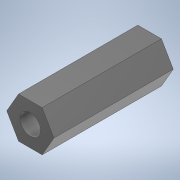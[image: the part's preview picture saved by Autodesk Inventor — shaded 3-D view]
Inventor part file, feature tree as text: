
AUTODESK INVENTOR PART (.ipt)
format: ipt  version: 2020 (Build 240168000, 168)  size: 103,936 bytes
history: native  units: mm
features: extrude x1, sketch x1
ambient origin geometry x8: Origin, YZ Plane, XZ Plane, XY Plane, X Axis, Y Axis, Z Axis, Center Point
bodies: Solid1 (feature_tree)
feature tree (2):
  extrude  "Extrusion1"  Depth=17.5mm
  sketch  "Sketch1"  dims[d0=3.0mm d1=3.0mm d2=17.5mm d3=0.0mm]
